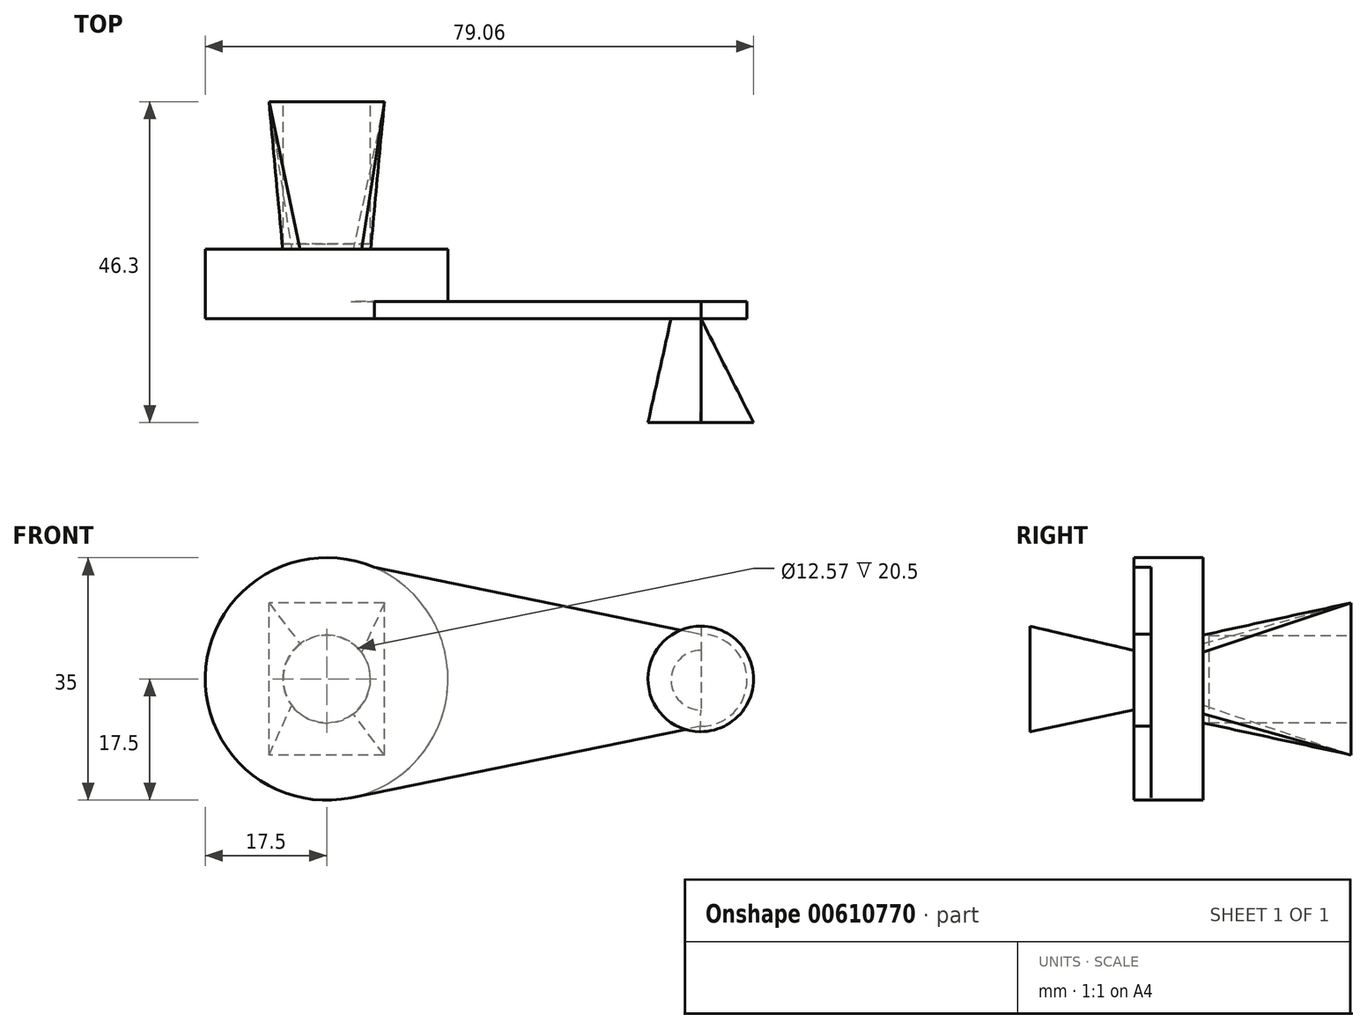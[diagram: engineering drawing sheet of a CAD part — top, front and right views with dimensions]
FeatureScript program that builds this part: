
annotation { "Feature Type Name" : "Feature", "Feature Type Description" : "" }
export const myFeature = defineFeature(function(context is Context, id is Id, definition is map)
    precondition{}
    {
        {
            var Q0;
            Q0=qCreatedBy(makeId("Front.planeOp"),FACE);
            var sketch = newSketch(context, id + "F0", { "sketchPlane" : qUnion([Q0])});
            skCircle(sketch, "E0", {"center": v(0, 0) * mm, "radius": 17.5 * mm});
            skSolve(sketch);
        }
        {
            var Q0;
            Q0=makeQuery(id+"F0.imprint","IMPRINT",FACE,{"disambiguationData":[TD([[makeQuery(id+"F0.imprint","IMPRINT",EDGE,{"derivedFrom":sQuery(id+"F0.wireOp",EDGE,"E0")}),1.0]])]});
            extrude(context, id + "F1", {"entities" : qUnion([Q0]), "depth" : 10 * mm, "offsetDistance" : 25 * mm});
        }
        {
            var Q0;
            Q0=makeQuery(id+"F1.opExtrude","CAP_FACE",FACE,{"disambiguationData":[OSD([sQuery(id+"F0.wireOp",EDGE,"E0")])],"isStart":false});
            var sketch = newSketch(context, id + "F2", { "sketchPlane" : qUnion([Q0])});
            skLineSegment(sketch, "E1", {"start": v(0, 17.5) * mm, "end": v(53.97, 6.47) * mm});
            skLineSegment(sketch, "E2", {"start": v(53.97, 6.47) * mm, "end": v(53.97, -6.83) * mm});
            skLineSegment(sketch, "E3", {"start": v(53.97, -6.83) * mm, "end": v(0, -17.86) * mm});
            skArc(sketch, "E4", {"start": v(53.97, -6.83) * mm, "mid": v(60.62, -0.18) * mm, "end": v(53.97, 6.47) * mm});
            skCircle(sketch, "E5", {"center": v(53.97, -0.18) * mm, "radius": 4.3 * mm});
            skSolve(sketch);
        }
        {
            var Q0;
            Q0=qCreatedBy(makeId("Front.planeOp"),FACE);
            cPlane(context, id + "F3", {"entities" : qUnion([Q0]), "cplaneType" : CPlaneType.OFFSET, "offset" : 25 * mm, "width" : 150 * mm, "height" : 150 * mm});
        }
        {
            var Q0;
            Q0=qCreatedBy(id+"F3.planeOp",FACE);
            var sketch = newSketch(context, id + "F4", { "sketchPlane" : qUnion([Q0])});
            skCircle(sketch, "E6", {"center": v(53.95, 0) * mm, "radius": 7.61 * mm});
            skSolve(sketch);
        }
        {
            var Q0;
            {var subQ2=sQuery(id+"F2.wireOp",EDGE,"E2");var subQ6=sQuery(id+"F2.wireOp",EDGE,"E5");var subQ10=makeQuery(id+"F2.imprint","INTERSECT",VERTEX,{"disambiguationData":[OD(0.0)],"derivedFrom":[subQ2,subQ6]});Q0=makeQuery(id+"F2.imprint","IMPRINT",FACE,{"disambiguationData":[TD([[makeQuery(id+"F2.imprint","IMPRINT",EDGE,{"disambiguationData":[TD([[subQ10,-1.0]])],"derivedFrom":subQ6}),-1.0]])]});}
            var Q1;
            {var subQ0=sQuery(id+"F2.wireOp",EDGE,"E5");var subQ1=sQuery(id+"F2.wireOp",EDGE,"E2");var subQ2=makeQuery(id+"F2.imprint","INTERSECT",VERTEX,{"disambiguationData":[OD(0.0)],"derivedFrom":[subQ1,subQ0]});Q1=makeQuery(id+"F2.imprint","IMPRINT",FACE,{"disambiguationData":[TD([[makeQuery(id+"F2.imprint","IMPRINT",EDGE,{"disambiguationData":[TD([[subQ2,-1.0]])],"derivedFrom":subQ1}),1.0]])]});}
            var Q2;
            {var subQ0=sQuery(id+"F2.wireOp",EDGE,"E5");var subQ1=sQuery(id+"F2.wireOp",EDGE,"E2");var subQ2=makeQuery(id+"F2.imprint","INTERSECT",VERTEX,{"disambiguationData":[OD(0.0)],"derivedFrom":[subQ1,subQ0]});Q2=makeQuery(id+"F2.imprint","IMPRINT",FACE,{"disambiguationData":[TD([[makeQuery(id+"F2.imprint","IMPRINT",EDGE,{"disambiguationData":[TD([[subQ2,-1.0]])],"derivedFrom":subQ1}),-1.0]])]});}
            var Q3;
            {var subQ0=sQuery(id+"F2.wireOp",EDGE,"E4");Q3=makeQuery(id+"F2.imprint","IMPRINT",FACE,{"disambiguationData":[TD([[makeQuery(id+"F2.imprint","IMPRINT",EDGE,{"derivedFrom":subQ0}),1.0]])]});}
            extrude(context, id + "F5", {"entities" : qUnion([Q0, Q1, Q2, Q3]), "operationType" : NewBodyOperationType.ADD, "oppositeDirection" : true, "depth" : 2.5 * mm, "offsetDistance" : 25 * mm});
        }
        {
            var Q1;
            Q1=makeQuery(id+"F4.imprint","IMPRINT",FACE,{"disambiguationData":[TD([[makeQuery(id+"F4.imprint","IMPRINT",EDGE,{"derivedFrom":sQuery(id+"F4.wireOp",EDGE,"E6")}),1.0]])]});
            var Q2;
            {var subQ0=sQuery(id+"F2.wireOp",EDGE,"E5");var subQ1=sQuery(id+"F2.wireOp",EDGE,"E2");var subQ2=makeQuery(id+"F2.imprint","INTERSECT",VERTEX,{"disambiguationData":[OD(0.0)],"derivedFrom":[subQ1,subQ0]});Q2=makeQuery(id+"F2.imprint","IMPRINT",FACE,{"disambiguationData":[TD([[makeQuery(id+"F2.imprint","IMPRINT",EDGE,{"disambiguationData":[TD([[subQ2,-1.0]])],"derivedFrom":subQ1}),-1.0]])]});}
            loft(context, id + "F6", {"operationType" : NewBodyOperationType.ADD, "sheetProfilesArray" : [{ "sheetProfileEntities" : qUnion([Q1]) }, { "sheetProfileEntities" : qUnion([Q2]) }]});
        }
        {
            var Q0;
            Q0=makeQuery(id+"F1.opExtrude","CAP_FACE",FACE,{"disambiguationData":[OSD([sQuery(id+"F0.wireOp",EDGE,"E0")])],"isStart":true});
            var sketch = newSketch(context, id + "F7", { "sketchPlane" : qUnion([Q0])});
            skCircle(sketch, "E7", {"center": v(0, 0) * mm, "radius": 6.35 * mm});
            skSolve(sketch);
        }
        {
            var Q0;
            Q0=qCreatedBy(makeId("Front.planeOp"),FACE);
            cPlane(context, id + "F8", {"entities" : qUnion([Q0]), "cplaneType" : CPlaneType.OFFSET, "offset" : 21.3 * mm, "oppositeDirection" : true, "width" : 150 * mm, "height" : 150 * mm});
        }
        {
            var Q0;
            Q0=qCreatedBy(id+"F8.planeOp",FACE);
            var sketch = newSketch(context, id + "F9", { "sketchPlane" : qUnion([Q0])});
            skLineSegment(sketch, "E8.bottom", {"start": v(8.32, -10.98) * mm, "end": v(-8.32, -10.98) * mm});
            skLineSegment(sketch, "E8.top", {"start": v(8.32, 10.98) * mm, "end": v(-8.32, 10.98) * mm});
            skLineSegment(sketch, "E8.left", {"start": v(8.32, -10.98) * mm, "end": v(8.32, 10.98) * mm});
            skLineSegment(sketch, "E8.right", {"start": v(-8.32, -10.98) * mm, "end": v(-8.32, 10.98) * mm});
            skPoint(sketch, "E8.middle", {"position": v(0, 0) * mm});
            skSolve(sketch);
        }
        {
            var Q1;
            Q1=makeQuery(id+"F9.imprint","IMPRINT",FACE,{"disambiguationData":[TD([[makeQuery(id+"F9.imprint","IMPRINT",EDGE,{"derivedFrom":sQuery(id+"F9.wireOp",EDGE,"E8.bottom")}),-1.0]])]});
            var Q2;
            Q2=makeQuery(id+"F7.imprint","IMPRINT",FACE,{"disambiguationData":[TD([[makeQuery(id+"F7.imprint","IMPRINT",EDGE,{"derivedFrom":sQuery(id+"F7.wireOp",EDGE,"E7")}),1.0]])]});
            loft(context, id + "F10", {"operationType" : NewBodyOperationType.ADD, "sheetProfilesArray" : [{ "sheetProfileEntities" : qUnion([Q1]) }, { "sheetProfileEntities" : qUnion([Q2]) }]});
        }
        {
            var Q0;
            Q0=makeQuery(id+"F10.opLoft","CAP_FACE",FACE,{"disambiguationData":[OSD([makeQuery(id+"F9.imprint","IMPRINT",FACE,{"disambiguationData":[TD([[makeQuery(id+"F9.imprint","IMPRINT",EDGE,{"derivedFrom":sQuery(id+"F9.wireOp",EDGE,"E8.bottom")}),-1.0]])]})])],"isStart":true});
            var sketch = newSketch(context, id + "F11", { "sketchPlane" : qUnion([Q0])});
            skCircle(sketch, "E9", {"center": v(0, 0) * mm, "radius": 6.29 * mm});
            skSolve(sketch);
        }
        {
            var Q0;
            Q0=makeQuery(id+"F11.imprint","IMPRINT",FACE,{"disambiguationData":[TD([[makeQuery(id+"F11.imprint","IMPRINT",EDGE,{"derivedFrom":sQuery(id+"F11.wireOp",EDGE,"E9")}),1.0]])]});
            extrude(context, id + "F12", {"entities" : qUnion([Q0]), "operationType" : NewBodyOperationType.REMOVE, "oppositeDirection" : true, "depth" : 20.5 * mm, "offsetDistance" : 25 * mm});
        }
    });
